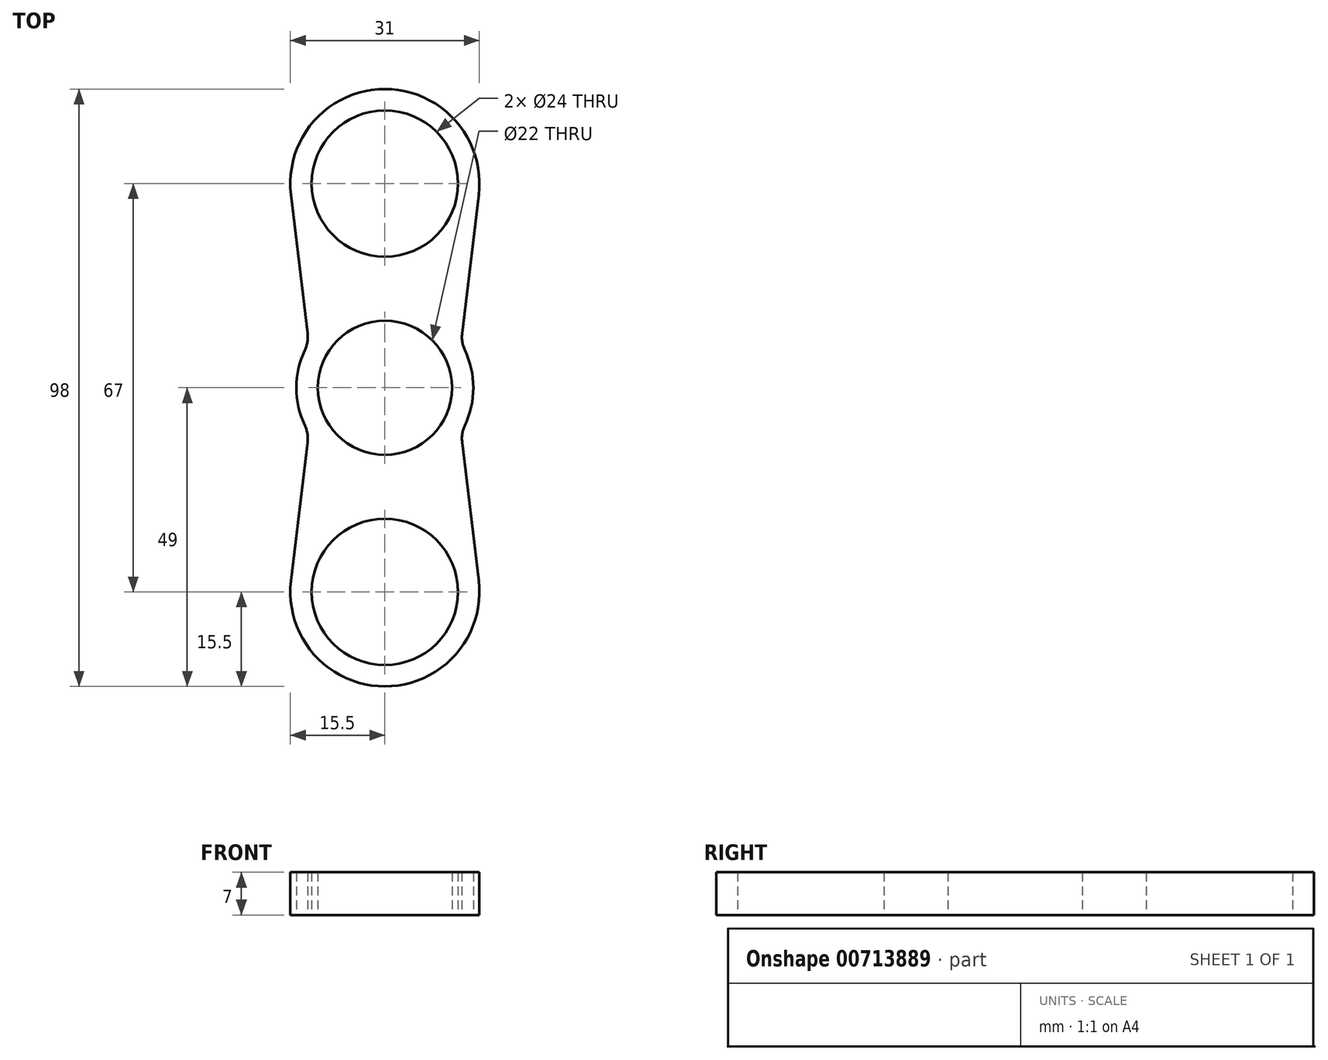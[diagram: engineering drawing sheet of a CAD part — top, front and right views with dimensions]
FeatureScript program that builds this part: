
annotation { "Feature Type Name" : "Feature", "Feature Type Description" : "" }
export const myFeature = defineFeature(function(context is Context, id is Id, definition is map)
    precondition{}
    {
        {
            var Q0;
            Q0=qCreatedBy(makeId("Top.planeOp"),FACE);
            var sketch = newSketch(context, id + "F0", { "sketchPlane" : qUnion([Q0])});
            skCircle(sketch, "E0", {"center": v(0, 0) * mm, "radius": 11 * mm});
            skArc(sketch, "E1", {"start": v(-13.12, 6.18) * mm, "mid": v(-14.5, 0) * mm, "end": v(-13.12, -6.18) * mm});
            skCircle(sketch, "E2", {"center": v(0, 33.5) * mm, "radius": 12 * mm});
            skArc(sketch, "E3", {"start": v(15.4, 31.66) * mm, "mid": v(0, 49) * mm, "end": v(-15.4, 31.66) * mm});
            skLineSegment(sketch, "E4", {"start": v(-15.4, 31.66) * mm, "end": v(-12.68, 8.9) * mm});
            skPoint(sketch, "E5.visualSharp", {"position": v(-12.5, 7.36) * mm});
            skArc(sketch, "E5.filletArc", {"start": v(-13.12, 6.18) * mm, "mid": v(-12.7, 7.5) * mm, "end": v(-12.68, 8.9) * mm});
            skLineSegment(sketch, "E6.MirrorCS", {"start": v(15.4, 31.66) * mm, "end": v(12.68, 8.9) * mm});
            skArc(sketch, "E7.MirrorCS", {"start": v(13.12, 6.18) * mm, "mid": v(12.7, 7.5) * mm, "end": v(12.68, 8.9) * mm});
            skPoint(sketch, "E8", {"position": v(13.12, 6.18) * mm});
            skPoint(sketch, "E9.orphan", {"position": v(12.5, 7.36) * mm});
            skArc(sketch, "E10.1.0", {"start": v(13.12, -6.18) * mm, "mid": v(12.7, -7.5) * mm, "end": v(12.68, -8.9) * mm});
            skLineSegment(sketch, "E10.1.1", {"start": v(15.4, -31.66) * mm, "end": v(12.68, -8.9) * mm});
            skArc(sketch, "E10.1.2", {"start": v(-15.4, -31.66) * mm, "mid": v(0, -49) * mm, "end": v(15.4, -31.66) * mm});
            skCircle(sketch, "E10.1.3", {"center": v(0, -33.5) * mm, "radius": 12 * mm});
            skLineSegment(sketch, "E10.1.4", {"start": v(-15.4, -31.66) * mm, "end": v(-12.68, -8.9) * mm});
            skArc(sketch, "E10.1.5", {"start": v(-13.12, -6.18) * mm, "mid": v(-12.7, -7.5) * mm, "end": v(-12.68, -8.9) * mm});
            skPoint(sketch, "E11", {"position": v(13.12, -6.18) * mm});
            skPoint(sketch, "E12", {"position": v(-13.12, -6.18) * mm});
            skArc(sketch, "E13.trimOffspring", {"start": v(13.12, -6.18) * mm, "mid": v(14.5, 0) * mm, "end": v(13.12, 6.18) * mm});
            skSolve(sketch);
        }
        {
            var Q0;
            Q0=makeQuery(id+"F0.imprint","IMPRINT",FACE,{"disambiguationData":[TD([[makeQuery(id+"F0.imprint","IMPRINT",EDGE,{"derivedFrom":sQuery(id+"F0.wireOp",EDGE,"E0")}),-1.0]])]});
            extrude(context, id + "F1", {"entities" : qUnion([Q0]), "depth" : 7 * mm, "offsetDistance" : 25 * mm});
        }
    });
